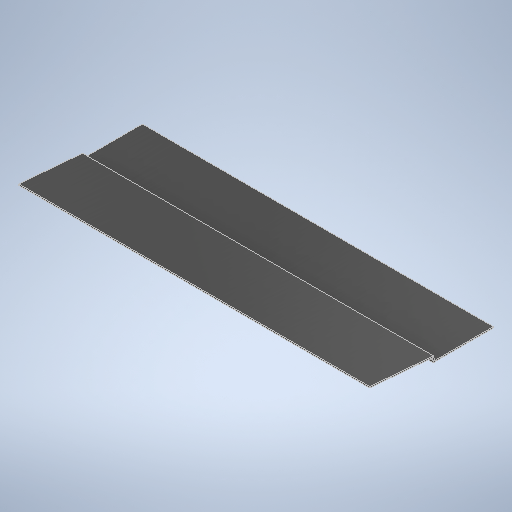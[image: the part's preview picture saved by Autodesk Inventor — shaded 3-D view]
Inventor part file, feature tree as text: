
AUTODESK INVENTOR PART (.ipt)
format: ipt  version: 2025.1 (Build 291241020, 241B)  size: 274,944 bytes
history: native  units: in
note: dims shown in document units (in); Inventor stores cm internally (conversion verified against a paired STEP export)
features: extrude x1, sketch x1
ambient origin geometry x8: Origin, YZ Plane, XZ Plane, XY Plane, X Axis, Y Axis, Z Axis, Center Point
bodies: Body1 (feature_tree)
feature tree (2):
  extrude  "Extrusion3"  Depth=0.125in
  sketch  "Sketch1"  dims[d0=23.408in d1=0.125in d2=0.265in d7=0.125in d8=0.237in d9=1.1431in d10=0.125in d11=0.7449in d12=0.125in d13=12.09in d18=0.125in d20=12.0907in d21=0.3425in d22=0.125in d23=0.125in d24=0.1549in d25=0.661in d28=0.125in d29=0.1254in d30=0.125in d32=0.125in d33=0.125in d34=5.625in d35=6.6451in d36=0.4476in d37=0.0449in d38=6.112in d39=36.45in d40=0.0in]
